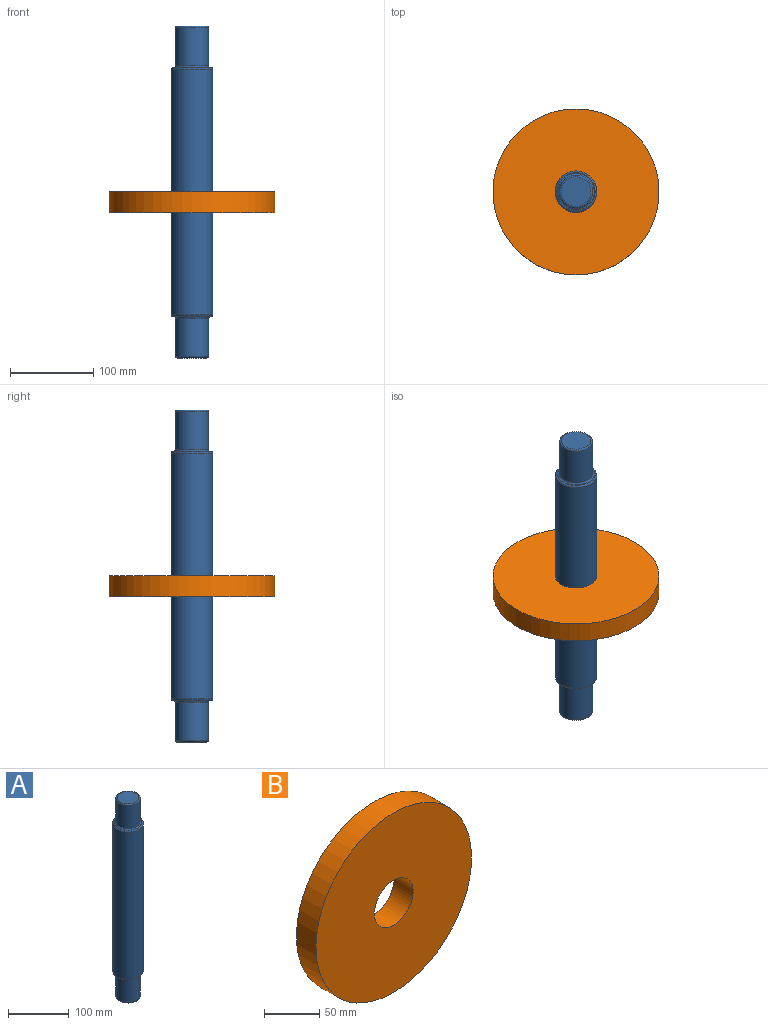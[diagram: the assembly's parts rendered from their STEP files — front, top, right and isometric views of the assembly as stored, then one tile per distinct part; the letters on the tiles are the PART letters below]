
ASSEMBLY  parts=2 mates=1
PART A: 13 faces, bbox 54.1x54.1x400 mm
  f0: cylinder r=25mm len=296mm, axis (0,0,1), area 46495.6mm2, adj f1,f12
  f1: torus R=23mm, axis (0,0,1), area 479.1mm2, adj f0,f2
  f2: plane 46x46mm, normal (0,0,1), area 141.4mm2, adj f1,f3
  f3: torus R=22mm, axis (0,0,1), area 409.1mm2, adj f2,f4
  f4: cylinder r=20mm len=46mm, axis (0,0,1), area 5780.5mm2, adj f3,f5
  f5: torus R=18mm, axis (0,0,1), area 380.4mm2, adj f4,f6
  f6: plane 36x36mm, normal (0,0,1), area 1017.9mm2, adj f5
  f7: plane 36x36mm, normal (0,0,-1), area 1017.9mm2, adj f8
  f8: torus R=18mm, axis (0,0,1), area 380.4mm2, adj f7,f9
  f9: cylinder r=20mm len=46mm, axis (0,0,1), area 5780.5mm2, adj f8,f10
  f10: torus R=22mm, axis (0,0,1), area 409.1mm2, adj f9,f11
  f11: plane 46x46mm, normal (0,0,-1), area 141.4mm2, adj f10,f12
  f12: torus R=23mm, axis (0,0,1), area 479.1mm2, adj f0,f11
PART B: 4 faces, bbox 200x25x200 mm
  f0: cylinder r=100mm len=200mm, axis (0,1,0), area 15708mm2, adj f1,f2
  f1: plane 200x200mm, normal (0,-1,0), area 29452.4mm2, adj f0,f3
  f2: plane 200x200mm, normal (0,1,0), area 29452.4mm2, adj f0,f3
  f3: cylinder r=25mm len=50mm, axis (0,-1,0), area 3927mm2, adj f1,f2
PLACE A t=(-228.3,-82.15,74.48)mm
PLACE B rot(axis=(-1,0,0),90deg) t=(-228.3,-82.15,61.98)mm
MATE revolute B.f0 <-> A.f0  axis (0,0,1) through (-228.3,-82.15,74.48)mm
